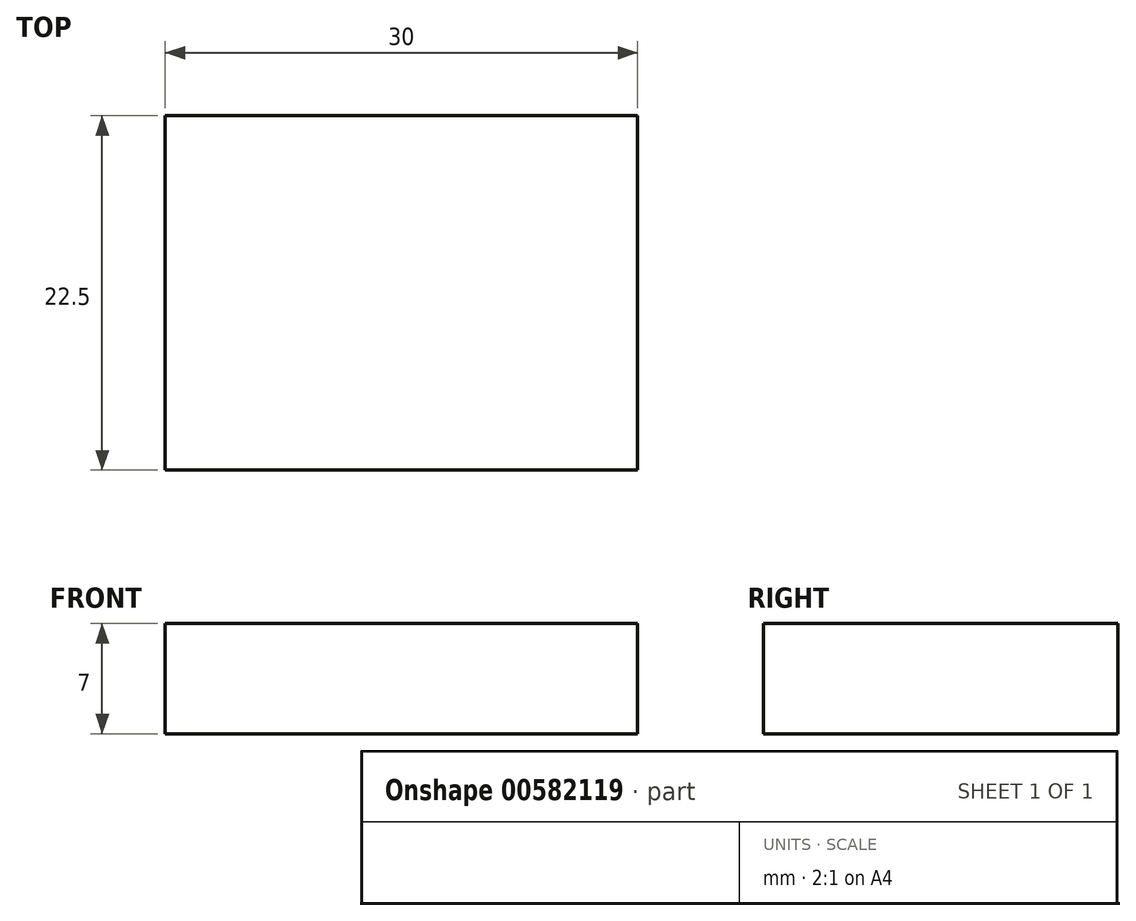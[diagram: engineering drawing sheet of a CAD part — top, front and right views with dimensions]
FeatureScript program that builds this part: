
annotation { "Feature Type Name" : "Feature", "Feature Type Description" : "" }
export const myFeature = defineFeature(function(context is Context, id is Id, definition is map)
    precondition{}
    {
        {
            var Q0;
            Q0=qCreatedBy(makeId("Top.planeOp"),FACE);
            var sketch = newSketch(context, id + "F0", { "sketchPlane" : qUnion([Q0])});
            skLineSegment(sketch, "E0.bottom", {"start": v(15, 11.25) * mm, "end": v(-15, 11.25) * mm});
            skLineSegment(sketch, "E0.top", {"start": v(15, -11.25) * mm, "end": v(-15, -11.25) * mm});
            skLineSegment(sketch, "E0.left", {"start": v(15, 11.25) * mm, "end": v(15, -11.25) * mm});
            skLineSegment(sketch, "E0.right", {"start": v(-15, 11.25) * mm, "end": v(-15, -11.25) * mm});
            skPoint(sketch, "E0.middle", {"position": v(0, 0) * mm});
            skSolve(sketch);
        }
        {
            var Q0;
            Q0 = qSketchRegion(id + "F0", true);
            extrude(context, id + "F1", {"entities" : qUnion([Q0]), "depth" : 7 * mm, "offsetDistance" : 25 * mm});
        }
    });
